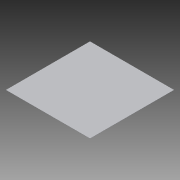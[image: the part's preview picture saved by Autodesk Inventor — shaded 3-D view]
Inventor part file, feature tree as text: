
AUTODESK INVENTOR PART (.ipt)
format: ipt  version: 2013 (Build 170138000, 138)  size: 73,728 bytes
history: native  units: in
note: dims shown in document units (in); Inventor stores cm internally (conversion verified against a paired STEP export)
features: sheet_metal_op x1, sketch x1, other x1
ambient origin geometry x8: Origin, YZ Plane, XZ Plane, XY Plane, X Axis, Y Axis, Z Axis, Center Point
bodies: Solid1 (feature_tree)
feature tree (3):
  sheet_metal_op  "Face1"
  sketch  "Sketch1"  dims[d0=48.0in d1=48.0in d2=0.0938in]
  other  "Plate1"
